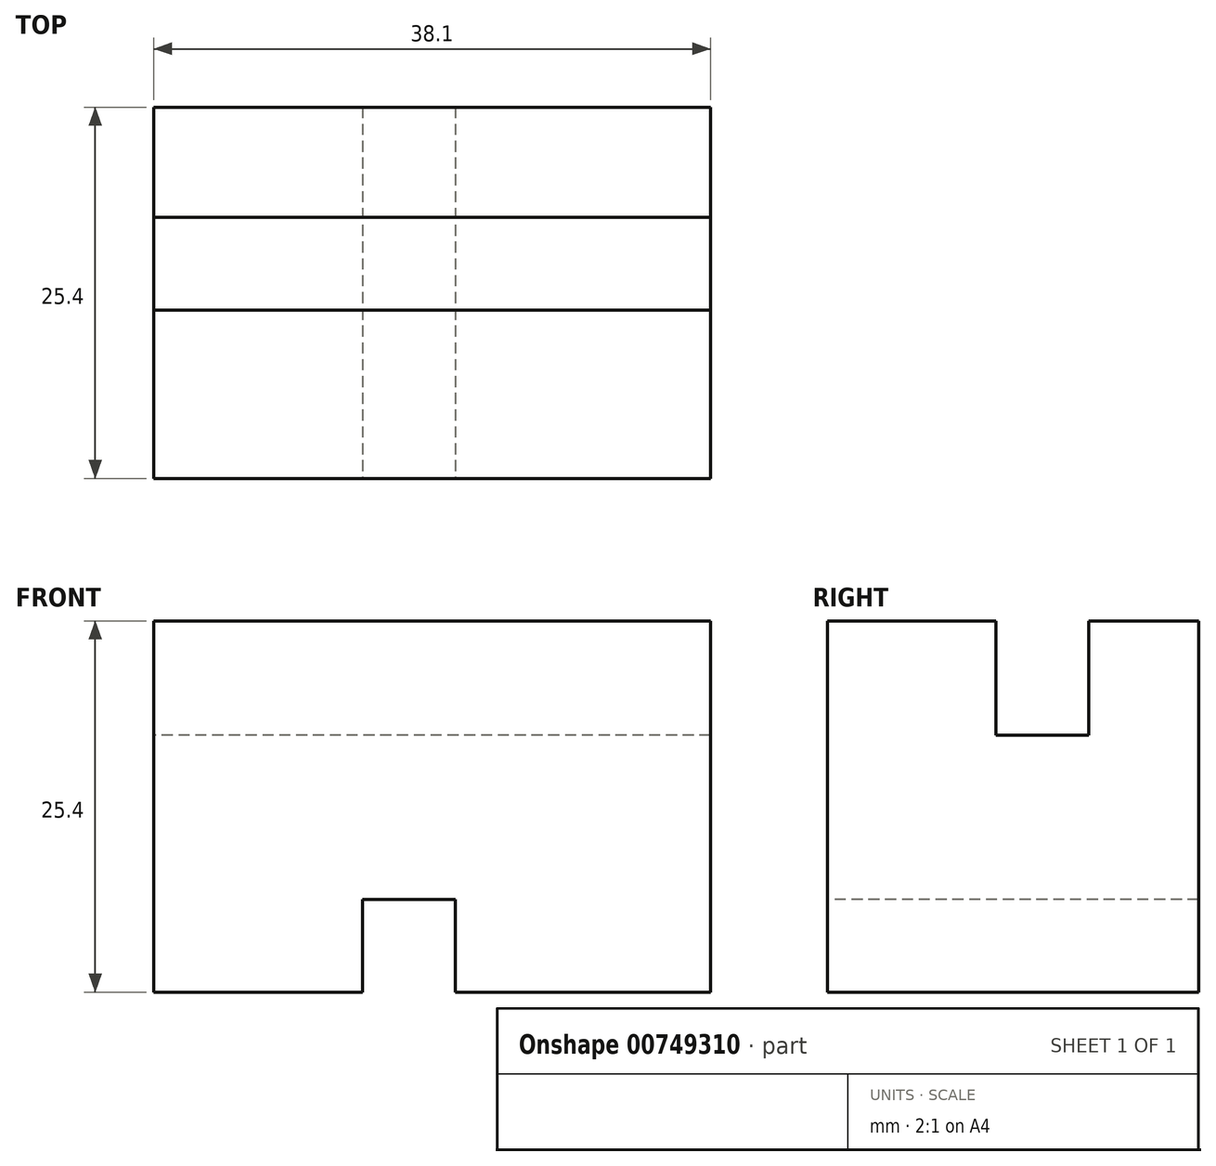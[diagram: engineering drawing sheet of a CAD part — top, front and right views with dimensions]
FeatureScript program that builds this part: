
annotation { "Feature Type Name" : "Feature", "Feature Type Description" : "" }
export const myFeature = defineFeature(function(context is Context, id is Id, definition is map)
    precondition{}
    {
        {
            var Q0;
            Q0=qCreatedBy(makeId("Front.planeOp"),FACE);
            var sketch = newSketch(context, id + "F0", { "sketchPlane" : qUnion([Q0])});
            skLineSegment(sketch, "E0", {"start": v(0, 0) * mm, "end": v(-38.1, 0) * mm});
            skLineSegment(sketch, "E1", {"start": v(-38.1, 0) * mm, "end": v(-38.1, 25.4) * mm});
            skLineSegment(sketch, "E2", {"start": v(-38.1, 25.4) * mm, "end": v(0, 25.4) * mm});
            skLineSegment(sketch, "E3", {"start": v(0, 25.4) * mm, "end": v(0, 0) * mm});
            skSolve(sketch);
        }
        {
            var Q0;
            Q0=makeQuery(id+"F0.imprint","IMPRINT",FACE,{"disambiguationData":[TD([[makeQuery(id+"F0.imprint","IMPRINT",EDGE,{"derivedFrom":sQuery(id+"F0.wireOp",EDGE,"E0")}),-1.0]])]});
            extrude(context, id + "F1", {"entities" : qUnion([Q0]), "depth" : 25.4 * mm, "offsetDistance" : 25.4 * mm});
        }
        {
            var Q0;
            Q0=makeQuery(id+"F1.opExtrude","SWEPT_FACE",FACE,{"disambiguationData":[OSD([sQuery(id+"F0.wireOp",EDGE,"E1")])]});
            var sketch = newSketch(context, id + "F2", { "sketchPlane" : qUnion([Q0])});
            skSolve(sketch);
        }
        {
            var Q0;
            {var subQ0=sQuery(id+"F0.wireOp",EDGE,"E1");Q0=makeQuery(id+"F2.imprint","IMPRINT",FACE,{"disambiguationData":[TD([[makeQuery(id+"F2.imprint","IMPRINT",EDGE,{"derivedFrom":makeQuery(id+"F1.opExtrude","CAP_EDGE",EDGE,{"disambiguationData":[OSD([subQ0])],"isStart":true})}),-1.0]])]});}
            var sketch = newSketch(context, id + "F3", { "sketchPlane" : qUnion([Q0])});
            skLineSegment(sketch, "E4", {"start": v(7.54, 26.23) * mm, "end": v(7.54, 17.6) * mm});
            skLineSegment(sketch, "E5", {"start": v(7.54, 17.6) * mm, "end": v(13.89, 17.6) * mm});
            skLineSegment(sketch, "E6", {"start": v(13.89, 17.6) * mm, "end": v(13.89, 26.03) * mm});
            skSolve(sketch);
        }
        {
            var Q0;
            {var subQ0=sQuery(id+"F3.wireOp",EDGE,"E5");Q0=makeQuery(id+"F3.imprint","IMPRINT",FACE,{"disambiguationData":[TD([[makeQuery(id+"F3.imprint","IMPRINT",EDGE,{"derivedFrom":subQ0}),1.0]])]});}
            extrude(context, id + "F4", {"entities" : qUnion([Q0]), "operationType" : NewBodyOperationType.REMOVE, "endBound" : BoundingType.THROUGH_ALL, "oppositeDirection" : true, "depth" : 25.4 * mm, "offsetDistance" : 25.4 * mm});
        }
        {
            var Q0;
            Q0=makeQuery(id+"F1.opExtrude","CAP_FACE",FACE,{"disambiguationData":[OSD([sQuery(id+"F0.wireOp",EDGE,"E0"),sQuery(id+"F0.wireOp",EDGE,"E1"),sQuery(id+"F0.wireOp",EDGE,"E2"),sQuery(id+"F0.wireOp",EDGE,"E3")])],"isStart":false});
            var sketch = newSketch(context, id + "F5", { "sketchPlane" : qUnion([Q0])});
            skLineSegment(sketch, "E7", {"start": v(-23.82, 0) * mm, "end": v(-23.82, 6.35) * mm});
            skLineSegment(sketch, "E8", {"start": v(-23.82, 6.35) * mm, "end": v(-17.47, 6.35) * mm});
            skLineSegment(sketch, "E9", {"start": v(-17.47, 6.35) * mm, "end": v(-17.47, 0) * mm});
            skSolve(sketch);
        }
        {
            var Q0;
            {var subQ0=sQuery(id+"F5.wireOp",EDGE,"E7");Q0=makeQuery(id+"F5.imprint","IMPRINT",FACE,{"disambiguationData":[TD([[makeQuery(id+"F5.imprint","IMPRINT",EDGE,{"derivedFrom":subQ0}),-1.0]])]});}
            extrude(context, id + "F6", {"entities" : qUnion([Q0]), "operationType" : NewBodyOperationType.REMOVE, "endBound" : BoundingType.THROUGH_ALL, "oppositeDirection" : true, "depth" : 25.4 * mm, "offsetDistance" : 25.4 * mm});
        }
    });
